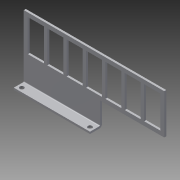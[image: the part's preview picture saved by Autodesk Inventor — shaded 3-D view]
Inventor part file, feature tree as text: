
AUTODESK INVENTOR PART (.ipt)
format: ipt  version: 2013 (Build 170138000, 138)  size: 241,152 bytes
history: native  units: in
note: dims shown in document units (in); Inventor stores cm internally (conversion verified against a paired STEP export)
features: sheet_metal_op x6, other x6, sketch x3
ambient origin geometry x8: Origin, YZ Plane, XZ Plane, XY Plane, X Axis, Y Axis, Z Axis, Center Point
bodies: Solid1 (feature_tree)
feature tree (15):
  sheet_metal_op  "Face1"
  sheet_metal_op  "Flange1"
  sheet_metal_op  "Face2"
  sketch  "Sketch1"  dims[d0=0.75in]
  other  "Plate1"
  sketch  "Sketch2"  dims[d1=4.75in]
  other  "Plate2"
  sheet_metal_op  "Bend1"
  sheet_metal_op  "Corner1"
  other  "Plate3"
  sheet_metal_op  "Bend2"
  sketch  "Sketch5"  dims[d2=0.266in d3=0.266in d4=4.25in d5=0.25in d6=0.5in d7=0.5in d8=0.125in d9=0.125in d10=0.0625in d11=0.25in d12=0.125in d13=1.5in d14=90.0deg d15=0.05in d16=0.5in d17=0.125in d18=0.125in d21=0.125in d22=0.125in d23=0.0625in d24=0.25in d25=0.125in d42=2.5in d43=4.0in d44=2.0in d45=1.0in d46=0.25in d47=0.25in d48=2.7559in d50=1.2083in d51=0.3937in d53=1.0in d55=0.125in d56=0.0in]
  other  "Cut2"
  other  "Definition1"
  other  "Cut1"
